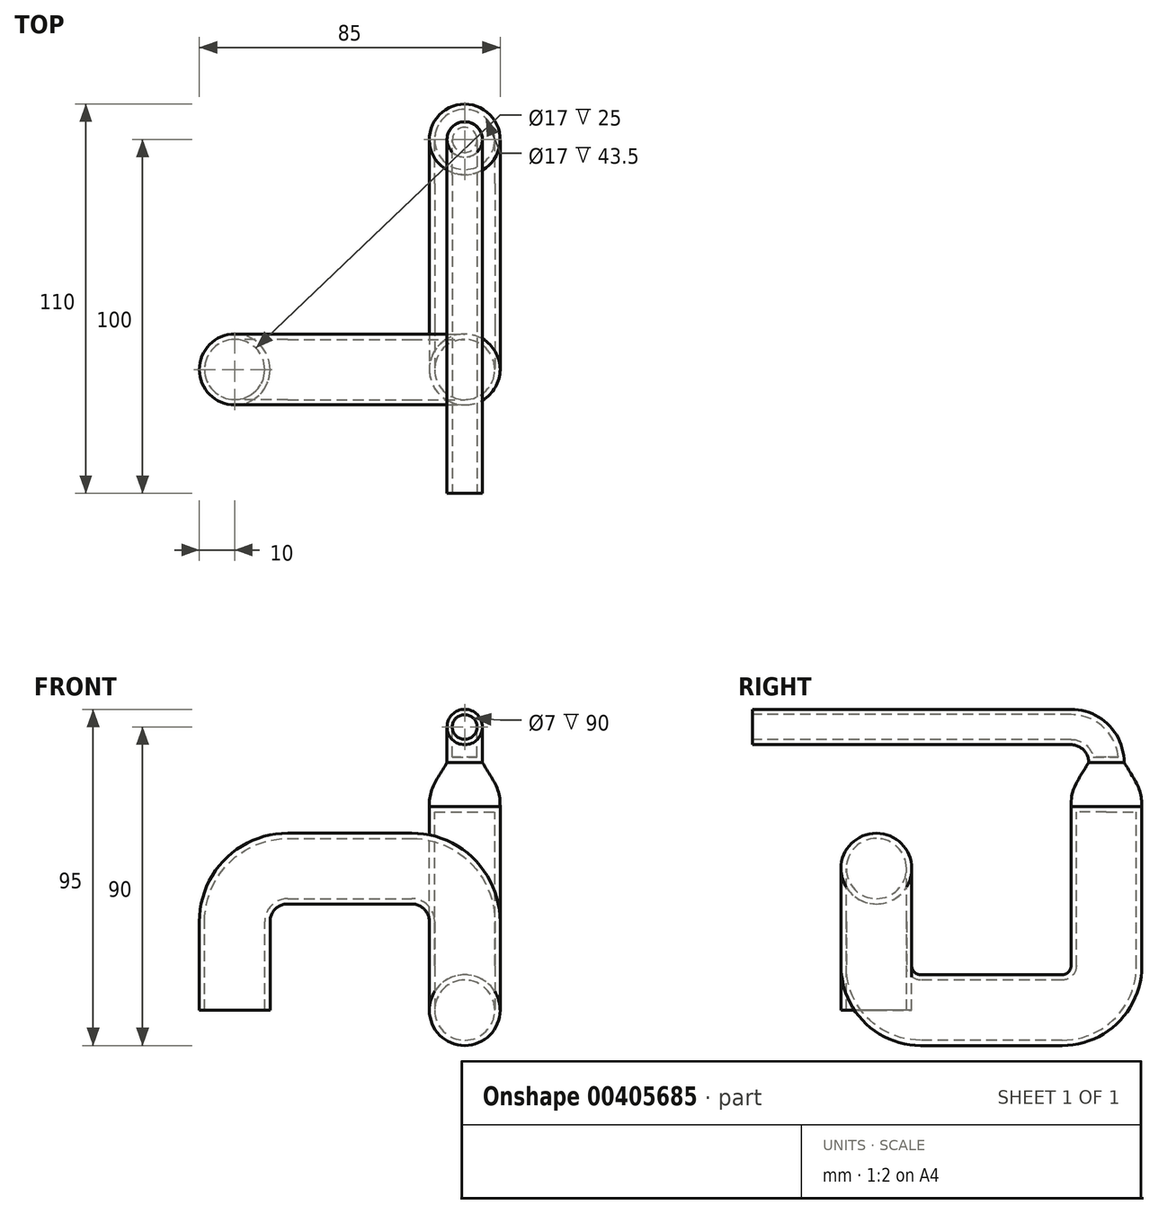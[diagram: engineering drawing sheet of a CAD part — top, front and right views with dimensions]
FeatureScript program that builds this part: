
annotation { "Feature Type Name" : "Feature", "Feature Type Description" : "" }
export const myFeature = defineFeature(function(context is Context, id is Id, definition is map)
    precondition{}
    {
        {
            var Q0;
            Q0=qCreatedBy(makeId("Top.planeOp"),FACE);
            var sketch = newSketch(context, id + "F0", { "sketchPlane" : qUnion([Q0])});
            skCircle(sketch, "E0", {"center": v(0, 0) * mm, "radius": 10 * mm});
            skLineSegment(sketch, "E1", {"start": v(0, 0) * mm, "end": v(65, 0) * mm});
            skPoint(sketch, "E2", {"position": v(65, 12.5) * mm});
            skSolve(sketch);
        }
        {
            var Q0;
            Q0=qCreatedBy(makeId("Front.planeOp"),FACE);
            var sketch = newSketch(context, id + "F1", { "sketchPlane" : qUnion([Q0])});
            skLineSegment(sketch, "E3.0", {"start": v(0, 0) * mm, "end": v(0, 25) * mm});
            skArc(sketch, "E4.0", {"start": v(15, 40) * mm, "mid": v(4.4, 35.6) * mm, "end": v(0, 25) * mm});
            skLineSegment(sketch, "E5.0", {"start": v(45, 40) * mm, "end": v(15, 40) * mm});
            skLineSegment(sketch, "E5.1", {"start": v(50, 40) * mm, "end": v(45, 40) * mm});
            skArc(sketch, "E5.2", {"start": v(50, 40) * mm, "mid": v(60.6, 35.6) * mm, "end": v(65, 25) * mm});
            skLineSegment(sketch, "E5.3", {"start": v(65, 25) * mm, "end": v(65, 12.5) * mm});
            skPoint(sketch, "E6", {"position": v(65, 12.5) * mm});
            skPoint(sketch, "E7.orphan", {"position": v(65, 0) * mm});
            skSolve(sketch);
        }
        {
            var Q0;
            Q0=makeQuery(id+"F0.imprint","IMPRINT",FACE,{"disambiguationData":[TD([[makeQuery(id+"F0.imprint","IMPRINT",EDGE,{"derivedFrom":sQuery(id+"F0.wireOp",EDGE,"E0")}),1.0]])]});
            var Q1;
            Q1=sQuery(id+"F1.wireOp",EDGE,"E3.0");
            var Q2;
            Q2=sQuery(id+"F1.wireOp",EDGE,"E4.0");
            var Q3;
            Q3=sQuery(id+"F1.wireOp",EDGE,"E5.0");
            var Q4;
            Q4=sQuery(id+"F1.wireOp",EDGE,"E5.2");
            var Q5;
            Q5=sQuery(id+"F1.wireOp",EDGE,"E5.3");
            var Q6;
            Q6=sQuery(id+"F1.wireOp",EDGE,"E5.1");
            var Q7;
            Q7=sQuery(id+"F0.wireOp",EDGE,"3Ayk6dHC-uAVS-XBJq-wXRU-8m2HeRQmatkH");
            var Q8;
            Q8 = qConstructionFilter(qBodyType(qCreatedBy(id + "F4" ,EDGE), BodyType.WIRE), ConstructionObject.NO);
            sweep(context, id + "F2", {"profiles" : qUnion([Q0]), "path" : qUnion([Q1, Q2, Q3, Q4, Q5, Q6, Q7, Q8])});
        }
        {
            var Q0;
            Q0=qCreatedBy(makeId("Right.planeOp"),FACE);
            var Q1;
            Q1 = qBodyType(qCreatedBy(id + "F4" ,EDGE), BodyType.WIRE);
            cPlane(context, id + "F3", {"entities" : qUnion([Q0, Q1]), "cplaneType" : CPlaneType.OFFSET, "offset" : 65 * mm, "width" : 150 * mm, "height" : 150 * mm});
        }
        {
            var Q0;
            Q0=qCreatedBy(id+"F3.planeOp",FACE);
            var sketch = newSketch(context, id + "F4", { "sketchPlane" : qUnion([Q0])});
            skPoint(sketch, "E8.0", {"position": v(0, 12.5) * mm});
            skPoint(sketch, "E9.0", {"position": v(12.5, 0) * mm});
            skArc(sketch, "E10", {"start": v(12.5, 0) * mm, "mid": v(3.66, 3.66) * mm, "end": v(0, 12.5) * mm});
            skLineSegment(sketch, "E11", {"start": v(12.5, 0) * mm, "end": v(52.5, 0) * mm});
            skArc(sketch, "E12", {"start": v(52.5, 0) * mm, "mid": v(61.34, 3.66) * mm, "end": v(65, 12.5) * mm});
            skLineSegment(sketch, "E13", {"start": v(65, 12.5) * mm, "end": v(65, 57.5) * mm});
            skLineSegment(sketch, "E14", {"start": v(65, 0) * mm, "end": v(65, 70) * mm});
            skPoint(sketch, "E14.endSnap0", {"position": v(65, 35) * mm});
            skArc(sketch, "E15", {"start": v(65, 70) * mm, "mid": v(62.07, 77.07) * mm, "end": v(55, 80) * mm});
            skLineSegment(sketch, "E16", {"start": v(55, 80) * mm, "end": v(-35, 80) * mm});
            skSolve(sketch);
        }
        {
            var Q0;
            Q0=qCreatedBy(makeId("Front.planeOp"),FACE);
            cPlane(context, id + "F5", {"entities" : qUnion([Q0]), "cplaneType" : CPlaneType.OFFSET, "offset" : 52.5 * mm, "oppositeDirection" : true, "width" : 150 * mm, "height" : 150 * mm});
        }
        {
            var Q0;
            Q0=qCreatedBy(id+"F5.planeOp",FACE);
            var sketch = newSketch(context, id + "F6", { "sketchPlane" : qUnion([Q0])});
            skPoint(sketch, "E17.0", {"position": v(65, 0) * mm});
            skCircle(sketch, "E18", {"center": v(65, 0) * mm, "radius": 10 * mm});
            skSolve(sketch);
        }
        {
            var Q0;
            Q0=makeQuery(id+"F6.imprint","IMPRINT",FACE,{"disambiguationData":[TD([[makeQuery(id+"F6.imprint","IMPRINT",EDGE,{"derivedFrom":sQuery(id+"F6.wireOp",EDGE,"E18")}),1.0]])]});
            var Q1;
            Q1=sQuery(id+"F4.wireOp",EDGE,"E11");
            var Q2;
            Q2=sQuery(id+"F4.wireOp",EDGE,"E10");
            sweep(context, id + "F7", {"operationType" : NewBodyOperationType.ADD, "profiles" : qUnion([Q0]), "path" : qUnion([Q1, Q2])});
        }
        {
            var Q0;
            Q0=makeQuery(id+"F7.opSweep","CAP_FACE",FACE,{"disambiguationData":[OSD([sQuery(id+"F4.wireOp",VERTEX,"E11.end"),sQuery(id+"F6.wireOp",EDGE,"E18")])],"isStart":true});
            var Q1;
            Q1=sQuery(id+"F4.wireOp",EDGE,"E12");
            var Q2;
            Q2=sQuery(id+"F4.wireOp",EDGE,"E13");
            sweep(context, id + "F8", {"operationType" : NewBodyOperationType.ADD, "profiles" : qUnion([Q0]), "path" : qUnion([Q1, Q2])});
        }
        {
            var Q0;
            Q0=qCreatedBy(makeId("Top.planeOp"),FACE);
            cPlane(context, id + "F9", {"entities" : qUnion([Q0]), "cplaneType" : CPlaneType.OFFSET, "offset" : 70 * mm, "width" : 150 * mm, "height" : 150 * mm});
        }
        {
            var Q0;
            Q0=qCreatedBy(id+"F9.planeOp",FACE);
            var sketch = newSketch(context, id + "F10", { "sketchPlane" : qUnion([Q0])});
            skPoint(sketch, "E19.0", {"position": v(65, 65) * mm});
            skCircle(sketch, "E20", {"center": v(65, 65) * mm, "radius": 5 * mm});
            skSolve(sketch);
        }
        {
            var Q0;
            Q0=makeQuery(id+"F10.imprint","IMPRINT",FACE,{"disambiguationData":[TD([[makeQuery(id+"F10.imprint","IMPRINT",EDGE,{"derivedFrom":sQuery(id+"F10.wireOp",EDGE,"E20")}),1.0]])]});
            var Q1;
            Q1=sQuery(id+"F4.wireOp",EDGE,"E15");
            var Q2;
            Q2=sQuery(id+"F4.wireOp",EDGE,"E16");
            sweep(context, id + "F11", {"profiles" : qUnion([Q0]), "path" : qUnion([Q1, Q2])});
        }
        {
            var Q0;
            Q0=makeQuery(id+"F8.opSweep","CAP_FACE",FACE,{"disambiguationData":[OSD([sQuery(id+"F4.wireOp",VERTEX,"E11.end"),sQuery(id+"F4.wireOp",VERTEX,"E13.end"),sQuery(id+"F6.wireOp",EDGE,"E18")])],"isStart":false});
            var Q1;
            Q1=makeQuery(id+"F11.opSweep","CAP_FACE",FACE,{"disambiguationData":[OSD([sQuery(id+"F4.wireOp",VERTEX,"E15.start"),sQuery(id+"F10.wireOp",EDGE,"E20")])],"isStart":true});
            loft(context, id + "F12", {"startCondition" : LoftEndDerivativeType.MATCH_CURVATURE, "startMagnitude" : 1, "endCondition" : LoftEndDerivativeType.MATCH_CURVATURE, "endMagnitude" : 0, "sheetProfilesArray" : [{ "sheetProfileEntities" : qUnion([Q0]) }, { "sheetProfileEntities" : qUnion([Q1]) }]});
        }
        {
            var Q0;
            Q0=makeQuery(id+"F11.opSweep","CAP_FACE",FACE,{"disambiguationData":[OSD([sQuery(id+"F4.wireOp",VERTEX,"E16.end"),sQuery(id+"F10.wireOp",EDGE,"E20")])],"isStart":false});
            var Q1;
            Q1=makeQuery(id+"F2.opSweep","CAP_FACE",FACE,{"disambiguationData":[OSD([sQuery(id+"F0.wireOp",EDGE,"E0"),sQuery(id+"F1.wireOp",VERTEX,"E3.0.start")])],"isStart":true});
            var Q2;
            Q2=makeQuery(id+"F2.opSweep","SWEPT_BODY",BODY,{"disambiguationData":[OSD([sQuery(id+"F0.wireOp",EDGE,"E0"),sQuery(id+"F1.wireOp",EDGE,"E3.0")])]});
            shell(context, id + "F13", {"entities" : qUnion([Q0, Q1]), "parts" : qUnion([Q2]), "thickness" : 1.5 * mm});
        }
    });
